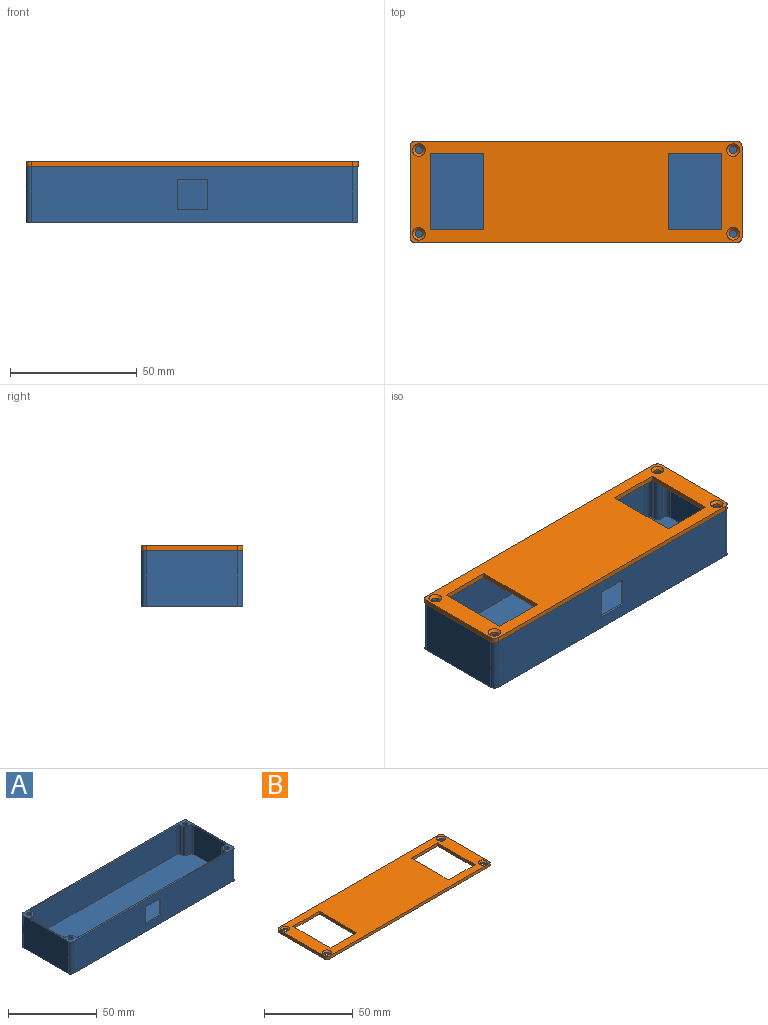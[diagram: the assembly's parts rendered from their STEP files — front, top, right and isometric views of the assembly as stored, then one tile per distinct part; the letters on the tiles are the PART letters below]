
ASSEMBLY  parts=2 mates=1
PART A: 47 faces, bbox 131x40x22 mm
  f0: plane 129x38mm, normal (0,0,1), area 4798.6mm2, adj f1,f2,f3,f4,f11,f12,f13,f14
  f1: plane 24x20mm, normal (-1,0,0), area 480mm2, adj f0,f9,f28,f30
  f2: plane 115x20mm, normal (0,1,0), area 2156mm2, adj f0,f9,f29,f33,f43,f44,f45,f46
  f3: plane 115x20mm, normal (0,-1,0), area 2300mm2, adj f0,f9,f32,f38
  f4: plane 24x20mm, normal (1,0,0), area 480mm2, adj f0,f9,f35,f37
  f5: plane 127x22mm, normal (0,1,0), area 2794mm2, adj f9,f10,f39,f42
  f6: plane 36x22mm, normal (-1,0,0), area 792mm2, adj f9,f10,f39,f40
  f7: plane 127x22mm, normal (0,-1,0), area 2650mm2, adj f9,f10,f40,f41,f43,f44,f45,f46
  f8: plane 36x22mm, normal (1,0,0), area 792mm2, adj f9,f10,f41,f42
  f9: plane 131x40mm, normal (0,0,1), area 409.7mm2, adj f1,f2,f3,f4,f5,f6,f7,f8
  f10: plane 131x40mm, normal (0,0,-1), area 5236.6mm2, adj f5,f6,f7,f8,f39,f40,f41,f42
  f11: plane 20x1mm, normal (1,0,0), area 20mm2, adj f0,f9,f36,f38
  f12: plane 20x1mm, normal (0,-1,0), area 20mm2, adj f0,f9,f36,f37
  f13: plane 20x1mm, normal (1,0,0), area 20mm2, adj f0,f9,f33,f34
  f14: plane 20x1mm, normal (0,1,0), area 20mm2, adj f0,f9,f34,f35
  f15: plane 20x1mm, normal (-1,0,0), area 20mm2, adj f0,f9,f31,f32
  f16: plane 20x1mm, normal (0,-1,0), area 20mm2, adj f0,f9,f30,f31
  f17: plane 20x1mm, normal (-1,0,0), area 20mm2, adj f0,f9,f27,f29
  f18: plane 20x1mm, normal (0,1,0), area 20mm2, adj f0,f9,f27,f28
  f19: cylinder r=1.5mm len=14mm, axis (0,0,1), area 131.9mm2, adj f9,f20
  f20: plane 3x3mm, normal (0,0,1), area 7.1mm2, adj f19
  f21: cylinder r=1.5mm len=14mm, axis (0,0,1), area 131.9mm2, adj f9,f22
  f22: plane 3x3mm, normal (0,0,1), area 7.1mm2, adj f21
  f23: cylinder r=1.5mm len=14mm, axis (0,0,1), area 131.9mm2, adj f9,f24
  f24: plane 3x3mm, normal (0,0,1), area 7.1mm2, adj f23
  f25: cylinder r=1.5mm len=14mm, axis (0,0,1), area 131.9mm2, adj f9,f26
  f26: plane 3x3mm, normal (0,0,1), area 7.1mm2, adj f25
  f27: cylinder r=2mm len=20mm, axis (0,0,1), area 62.8mm2, adj f0,f9,f17,f18
  f28: cylinder r=2mm len=20mm, axis (0,0,1), area 62.8mm2, adj f0,f1,f9,f18
  f29: cylinder r=2mm len=20mm, axis (0,0,1), area 62.8mm2, adj f0,f2,f9,f17
  f30: cylinder r=2mm len=20mm, axis (0,0,-1), area 62.8mm2, adj f0,f1,f9,f16
  f31: cylinder r=2mm len=20mm, axis (0,0,1), area 62.8mm2, adj f0,f9,f15,f16
  f32: cylinder r=2mm len=20mm, axis (0,0,1), area 62.8mm2, adj f0,f3,f9,f15
  f33: cylinder r=2mm len=20mm, axis (0,0,-1), area 62.8mm2, adj f0,f2,f9,f13
  f34: cylinder r=2mm len=20mm, axis (0,0,1), area 62.8mm2, adj f0,f9,f13,f14
  f35: cylinder r=2mm len=20mm, axis (0,0,1), area 62.8mm2, adj f0,f4,f9,f14
  f36: cylinder r=2mm len=20mm, axis (0,0,1), area 62.8mm2, adj f0,f9,f11,f12
  f37: cylinder r=2mm len=20mm, axis (0,0,-1), area 62.8mm2, adj f0,f4,f9,f12
  f38: cylinder r=2mm len=20mm, axis (0,0,-1), area 62.8mm2, adj f0,f3,f9,f11
  f39: cylinder r=2mm len=22mm, axis (0,0,1), area 69.1mm2, adj f5,f6,f9,f10
  f40: cylinder r=2mm len=22mm, axis (0,0,-1), area 69.1mm2, adj f6,f7,f9,f10
  f41: cylinder r=2mm len=22mm, axis (0,0,1), area 69.1mm2, adj f7,f8,f9,f10
  f42: cylinder r=2mm len=22mm, axis (0,0,-1), area 69.1mm2, adj f5,f8,f9,f10
  f43: plane 12x1mm, normal (1,0,0), area 12mm2, adj f2,f7,f44,f46
  f44: plane 12x1mm, normal (0,0,1), area 12mm2, adj f2,f7,f43,f45
  f45: plane 12x1mm, normal (-1,0,0), area 12mm2, adj f2,f7,f44,f46
  f46: plane 12x1mm, normal (0,0,-1), area 12mm2, adj f2,f7,f43,f45
PART B: 26 faces, bbox 131x40x2 mm
  f0: plane 127x2mm, normal (0,-1,0), area 254mm2, adj f4,f5,f14,f17
  f1: plane 36x2mm, normal (1,0,0), area 72mm2, adj f4,f5,f14,f15
  f2: plane 127x2mm, normal (0,1,0), area 254mm2, adj f4,f5,f15,f16
  f3: plane 36x2mm, normal (-1,0,0), area 72mm2, adj f4,f5,f16,f17
  f4: plane 131x40mm, normal (0,0,1), area 3898mm2, adj f0,f1,f2,f3,f10,f11,f12,f13
  f5: plane 131x40mm, normal (0,0,-1), area 3948.3mm2, adj f0,f1,f2,f3,f6,f7,f8,f9
  f6: cylinder r=1.5mm len=3mm, axis (0,0,1), area 9.4mm2, adj f5,f13
  f7: cylinder r=1.5mm len=3mm, axis (0,0,1), area 9.4mm2, adj f5,f12
  f8: cylinder r=1.5mm len=3mm, axis (0,0,1), area 9.4mm2, adj f5,f11
  f9: cylinder r=1.5mm len=3mm, axis (0,0,1), area 9.4mm2, adj f5,f10
  f10: cone r=1.5mm half-angle=45deg, axis (0,0,1), area 17.8mm2, adj f4,f9
  f11: cone r=1.5mm half-angle=45deg, axis (0,0,1), area 17.8mm2, adj f4,f8
  f12: cone r=1.5mm half-angle=45deg, axis (0,0,1), area 17.8mm2, adj f4,f7
  f13: cone r=1.5mm half-angle=45deg, axis (0,0,1), area 17.8mm2, adj f4,f6
  f14: cylinder r=2mm len=2mm, axis (0,0,1), area 6.3mm2, adj f0,f1,f4,f5
  f15: cylinder r=2mm len=2mm, axis (0,0,-1), area 6.3mm2, adj f1,f2,f4,f5
  f16: cylinder r=2mm len=2mm, axis (0,0,1), area 6.3mm2, adj f2,f3,f4,f5
  f17: cylinder r=2mm len=2mm, axis (0,0,-1), area 6.3mm2, adj f0,f3,f4,f5
  f18: plane 30x2mm, normal (-1,0,0), area 60mm2, adj f4,f5,f19,f21
  f19: plane 21x2mm, normal (0,-1,0), area 42mm2, adj f4,f5,f18,f20
  f20: plane 30x2mm, normal (1,0,0), area 60mm2, adj f4,f5,f19,f21
  f21: plane 21x2mm, normal (0,1,0), area 42mm2, adj f4,f5,f18,f20
  f22: plane 30x2mm, normal (-1,0,0), area 60mm2, adj f4,f5,f23,f25
  f23: plane 21x2mm, normal (0,-1,0), area 42mm2, adj f4,f5,f22,f24
  f24: plane 30x2mm, normal (1,0,0), area 60mm2, adj f4,f5,f23,f25
  f25: plane 21x2mm, normal (0,1,0), area 42mm2, adj f4,f5,f22,f24
PLACE A t=(-0.21,31.74,3.11)mm fixed
PLACE B t=(-0.41,94.13,25.11)mm
MATE slider A.f23 <-> B.f8  axis (0,0,1) through (61.59,48.5,25.11)mm
